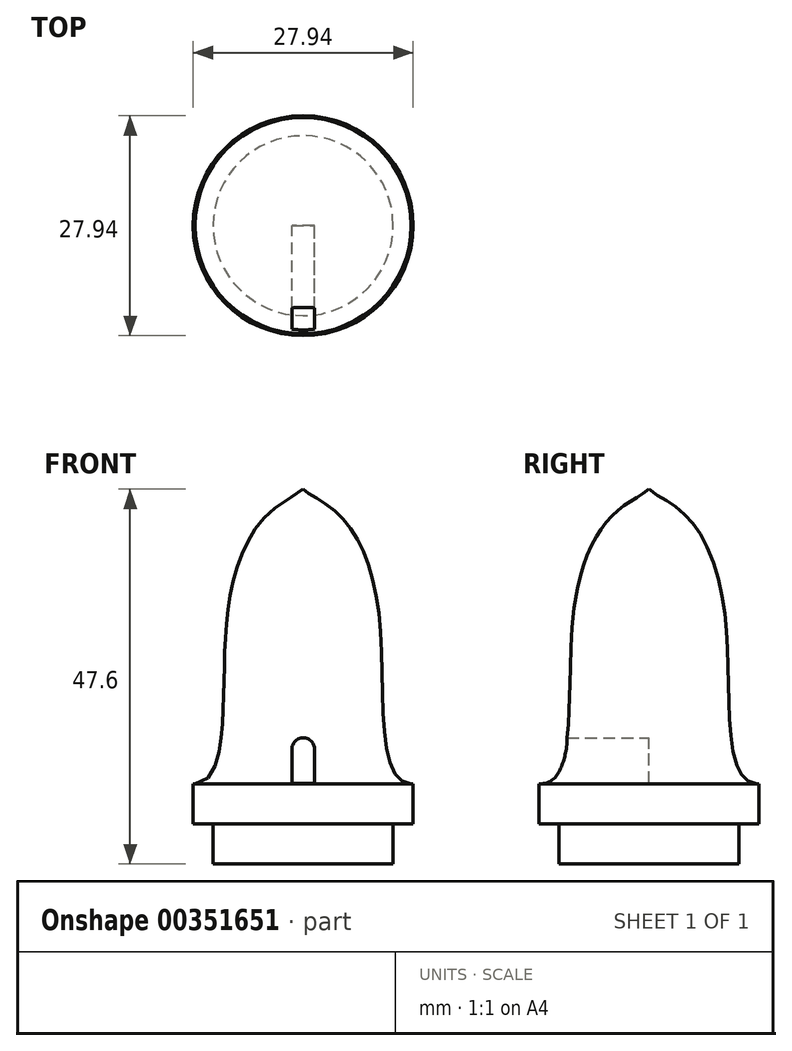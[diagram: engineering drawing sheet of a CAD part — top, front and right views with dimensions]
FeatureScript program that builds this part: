
annotation { "Feature Type Name" : "Feature", "Feature Type Description" : "" }
export const myFeature = defineFeature(function(context is Context, id is Id, definition is map)
    precondition{}
    {
        {
            var Q0;
            Q0=qCreatedBy(makeId("Front.planeOp"),FACE);
            var sketch = newSketch(context, id + "F0", { "sketchPlane" : qUnion([Q0])});
            skLineSegment(sketch, "E0.bottom", {"start": v(0, 0) * mm, "end": v(11.43, 0) * mm});
            skLineSegment(sketch, "E0.top", {"start": v(0, -5.08) * mm, "end": v(11.43, -5.08) * mm});
            skLineSegment(sketch, "E0.left", {"start": v(0, 0) * mm, "end": v(0, -5.08) * mm});
            skLineSegment(sketch, "E0.right", {"start": v(11.43, 0) * mm, "end": v(11.43, -5.08) * mm});
            skLineSegment(sketch, "E1.bottom", {"start": v(0, 0) * mm, "end": v(13.97, 0) * mm});
            skLineSegment(sketch, "E1.top", {"start": v(0, 5.08) * mm, "end": v(13.97, 5.08) * mm});
            skLineSegment(sketch, "E1.left", {"start": v(0, 0) * mm, "end": v(0, 5.08) * mm});
            skLineSegment(sketch, "E1.right", {"start": v(13.97, 0) * mm, "end": v(13.97, 5.08) * mm});
            skLineSegment(sketch, "E2", {"start": v(0, 5.08) * mm, "end": v(0, 43.18) * mm});
            skFitSpline(sketch, "E3", {"points": [v(0, 43.18) * mm, v(3.35, 40.3) * mm, v(9.8, 24.76) * mm, v(13.97, 5.08) * mm, v(33, 37.2) * mm, v(0, 43.18) * mm]});
            skSolve(sketch);
        }
        {
            var Q0;
            Q0=makeQuery(id+"F0.imprint","IMPRINT",FACE,{"disambiguationData":[TD([[makeQuery(id+"F0.imprint","IMPRINT",EDGE,{"derivedFrom":sQuery(id+"F0.wireOp",EDGE,"E0.bottom")}),-1.0]])]});
            var Q1;
            {var subQ0=sQuery(id+"F0.wireOp",EDGE,"E3");var subQ1=sQuery(id+"F0.wireOp",EDGE,"E2");var subQ2=makeQuery(id+"F0.imprint","INTERSECT",VERTEX,{"disambiguationData":[OD(0.0)],"derivedFrom":[subQ1,subQ0]});Q1=makeQuery(id+"F0.imprint","IMPRINT",FACE,{"disambiguationData":[TD([[makeQuery(id+"F0.imprint","IMPRINT",EDGE,{"disambiguationData":[TD([[subQ2,1.0]])],"derivedFrom":subQ1}),1.0]])]});}
            var Q2;
            {var subQ0=sQuery(id+"F0.wireOp",EDGE,"E2");var subQ3=sQuery(id+"F0.wireOp",EDGE,"E3");var subQ5=makeQuery(id+"F0.imprint","INTERSECT",VERTEX,{"disambiguationData":[OD(1.0)],"derivedFrom":[subQ0,subQ3]});Q2=makeQuery(id+"F0.imprint","IMPRINT",FACE,{"disambiguationData":[TD([[makeQuery(id+"F0.imprint","IMPRINT",EDGE,{"disambiguationData":[TD([[subQ5,-1.0]])],"derivedFrom":subQ3}),-1.0]])]});}
            var Q3;
            {var subQ0=sQuery(id+"F0.wireOp",EDGE,"E3");var subQ1=sQuery(id+"F0.wireOp",EDGE,"E1.top");var subQ3=makeQuery(id+"F0.imprint","INTERSECT",VERTEX,{"derivedFrom":[subQ1,subQ0]});Q3=makeQuery(id+"F0.imprint","IMPRINT",FACE,{"disambiguationData":[TD([[makeQuery(id+"F0.imprint","IMPRINT",EDGE,{"disambiguationData":[TD([[subQ3,-1.0]])],"derivedFrom":subQ1}),-1.0]])]});}
            var Q4;
            Q4=makeQuery(id+"F0.imprint","IMPRINT",FACE,{"disambiguationData":[TD([[makeQuery(id+"F0.imprint","IMPRINT",EDGE,{"derivedFrom":sQuery(id+"F0.wireOp",EDGE,"E0.bottom")}),1.0]])]});
            var Q5;
            Q5=sQuery(id+"F0.wireOp",EDGE,"E2");
            revolve(context, id + "F1", {"entities" : qUnion([Q0, Q1, Q2, Q3, Q4]), "axis" : qUnion([Q5]), "revolveType" : RevolveType.FULL});
        }
        {
            var Q0;
            Q0=makeQuery(id+"F1.opRevolve","SWEPT_BODY",BODY,{"disambiguationData":[OSD([sQuery(id+"F0.wireOp",EDGE,"E2"),sQuery(id+"F0.wireOp",EDGE,"E3")])]});
            deleteBodies(context, id + "F2", {"entities" : qUnion([Q0])});
        }
        {
            var Q0;
            Q0=qCreatedBy(makeId("Front.planeOp"),FACE);
            var sketch = newSketch(context, id + "F3", { "sketchPlane" : qUnion([Q0])});
            skLineSegment(sketch, "E4", {"start": v(0, 33.13) * mm, "end": v(0, 0) * mm});
            skLineSegment(sketch, "E5", {"start": v(0, 5.15) * mm, "end": v(3.75, 5.15) * mm});
            skLineSegment(sketch, "E6", {"start": v(3.75, 5.15) * mm, "end": v(-4.5, 5.15) * mm});
            skLineSegment(sketch, "E7.bottom", {"start": v(1.44, 5.15) * mm, "end": v(-1.44, 5.15) * mm});
            skLineSegment(sketch, "E7.top", {"start": v(1.44, 9.49) * mm, "end": v(-1.44, 9.49) * mm});
            skLineSegment(sketch, "E7.left", {"start": v(1.44, 5.15) * mm, "end": v(1.44, 9.49) * mm});
            skLineSegment(sketch, "E7.right", {"start": v(-1.44, 5.15) * mm, "end": v(-1.44, 9.49) * mm});
            skPoint(sketch, "E7.middle", {"position": v(0, 7.32) * mm});
            skArc(sketch, "E8", {"start": v(-1.44, 9.49) * mm, "mid": v(0, 10.92) * mm, "end": v(1.44, 9.49) * mm});
            skSolve(sketch);
        }
        {
            var Q0;
            {var subQ0=sQuery(id+"F3.wireOp",EDGE,"E7.top");var subQ1=sQuery(id+"F3.wireOp",EDGE,"E4");var subQ2=makeQuery(id+"F3.imprint","INTERSECT",VERTEX,{"derivedFrom":[subQ1,subQ0]});var subQ5=makeQuery(id+"F3.imprint","IMPRINT",EDGE,{"disambiguationData":[TD([[subQ2,1.0]])],"derivedFrom":subQ1});var subQ6=sQuery(id+"F3.wireOp",EDGE,"E7.left");var subQ9=sQuery(id+"F3.wireOp",EDGE,"E7.right");Q0=qUnion([makeQuery(id+"F3.imprint","IMPRINT",FACE,{"disambiguationData":[TD([[makeQuery(id+"F3.imprint","IMPRINT",EDGE,{"derivedFrom":subQ6}),1.0]])]}),makeQuery(id+"F3.imprint","IMPRINT",FACE,{"disambiguationData":[TD([[makeQuery(id+"F3.imprint","IMPRINT",EDGE,{"derivedFrom":subQ9}),-1.0]])]}),makeQuery(id+"F3.imprint","IMPRINT",FACE,{"disambiguationData":[TD([[subQ5,-1.0]])]}),makeQuery(id+"F3.imprint","IMPRINT",FACE,{"disambiguationData":[TD([[subQ5,1.0]])]})]);}
            extrude(context, id + "F4", {"entities" : qUnion([Q0]), "operationType" : NewBodyOperationType.REMOVE, "depth" : 25.4 * mm});
        }
    });
